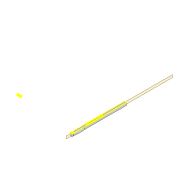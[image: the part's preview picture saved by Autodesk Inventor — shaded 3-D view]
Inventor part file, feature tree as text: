
AUTODESK INVENTOR PART (.ipt)
format: ipt  version: 2022 (Build 260153000, 153)  size: 133,120 bytes
history: native  units: mm
features: sketch x4, extrude x2, projected_geometry x2
ambient origin geometry x8: Origin, YZ Plane, XZ Plane, XY Plane, X Axis, Y Axis, Z Axis, Center Point
bodies: Solid1 (feature_tree)
feature tree (8):
  extrude  "Extrusion1"  Depth=8.0mm
  sketch  "Sketch2"  dims[d2=3.0mm d3=3.0mm]
  extrude  "Extrusion2"  Depth=3.0mm
  sketch  "Sketch4"  dims[d12=3.0mm d13=50.8mm d14=100.0mm d15=40.0mm d16=200.0mm d17=200.0mm d18=20.0mm d19=0.0mm d20=0.5mm d21=0.872665mm]
  sketch  "Sketch1"  dims[d0=319.927mm d1=8.0mm]
  projected_geometry  "Projected Loop1"
  sketch  "Sketch3"  dims[d4=8.0mm d5=0.0mm]
  projected_geometry  "Projected Loop2"
